# Revit family: FP-Revit20-en-OB60SD9PX1-OB60SD9X1-Oven-0-9000XXXXA-CN
name_source: partatom
category: Specialty Equipment
units: mm (PartAtom-declared; Revit-internal decimal feet)

## family parameters
Always vertical = Yes
Cut with Voids When Loaded = Yes
OmniClass Number = 23.40.40.14.17.11
OmniClass Title = Cookers, Ovens, Stoves
Part Type = Normal
Room Calculation Point = No
Round Connector Dimension = Use Diameter
Shared = No
Work Plane-Based = No

## types (2) — shared parameters
Cavity - Depth = 550 mm
Cavity - Height = 600 mm  [stored 1.9685 ft]
Cavity - Width = 600 mm  [stored 1.9685 ft]
Chassis - Depth = 545 mm  [stored 1.78806 ft]
Chassis - Height = 575 mm
Chassis - Width = 556 mm  [stored 1.82415 ft]
Connector Note - Electrical = 220 -240 V, 50 Hz, 15 A
Description = 60cm Built-In Oven
Manufacturer = Fisher & Paykel Appliances
Material - Body = Fisher & Paykel - Grey
Material - Buttons and Dials = Fisher & Paykel - Stainless Steel
Material - Glass = Fisher & Paykel - Glass, Black
Material - Handle = Fisher & Paykel - Stainless Steel
Material - Structure = Fisher & Paykel - Black
Material - Trim = Fisher & Paykel - Stainless Steel
Product - Depth = 565 mm  [stored 1.85367 ft]
Product - Height = 598 mm  [stored 1.96194 ft]
Product - Width = 596 mm  [stored 1.95538 ft]
URL = www.fisherpaykel.com
Visibility - Clearance Required = Yes
zero-valued in all types: Default Elevation

## per-type parameters (varying)
| type | Model |
| OB60SD9PX1 | OB60SD9PX1 |
| OB60SD9X1 | OB60SD9X1
OB60SD9X1
OB60SD9X1
OB60SD9X1 |

note: [stored X ft] marks values corroborated as IEEE doubles in the binary element streams (Revit-internal decimal feet)

## geometry (parser evidence)
native form markers: Sweep x6
no freeform markers — native parametric forms only
